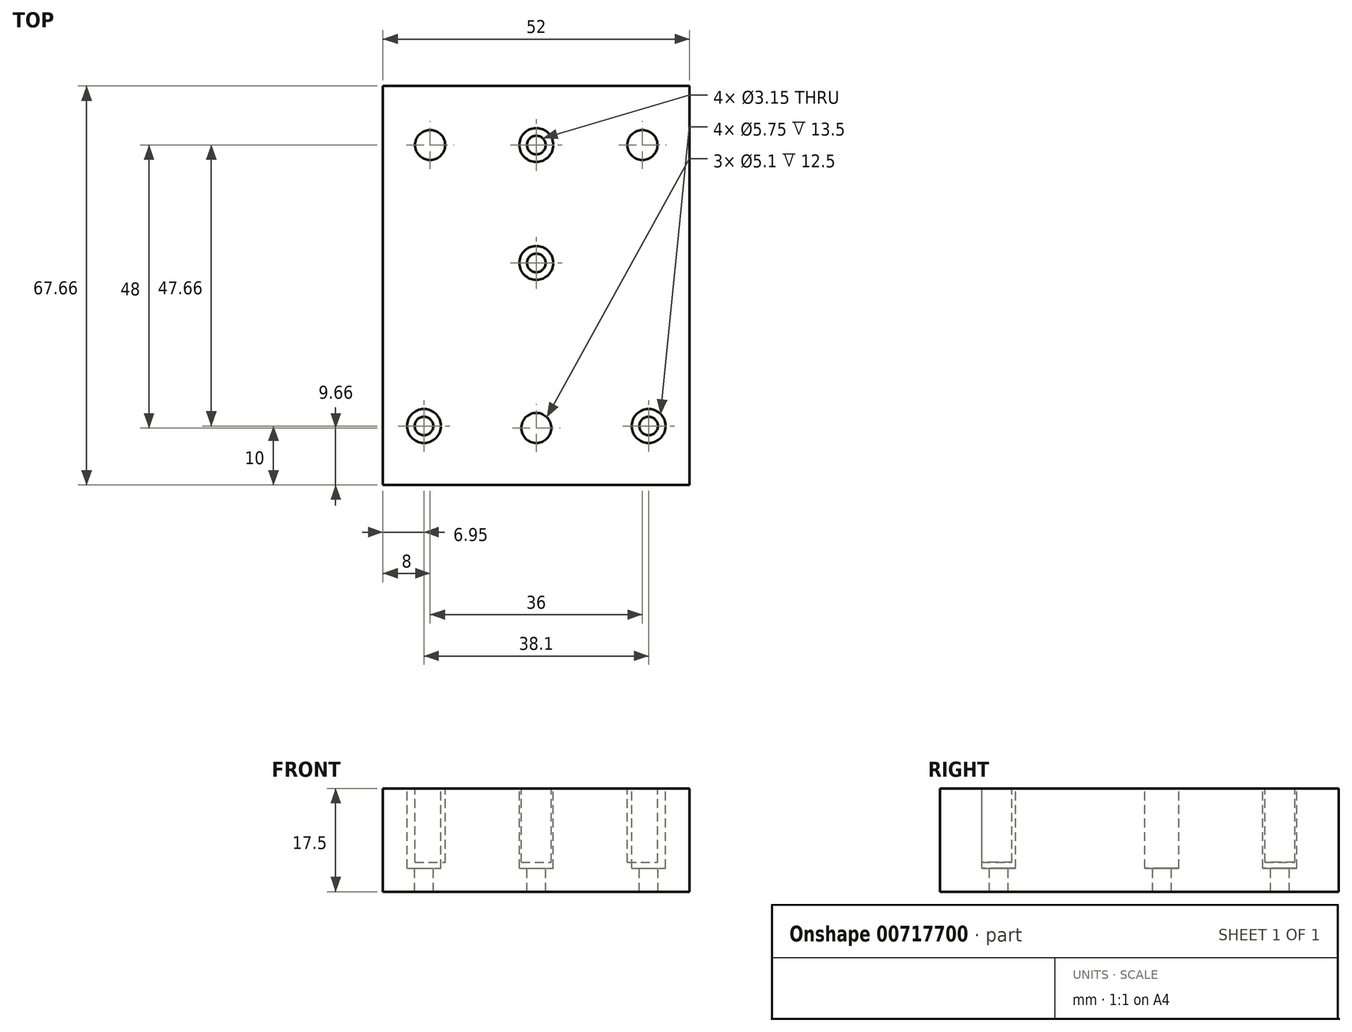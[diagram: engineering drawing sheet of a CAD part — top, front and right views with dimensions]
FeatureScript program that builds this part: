
annotation { "Feature Type Name" : "Feature", "Feature Type Description" : "" }
export const myFeature = defineFeature(function(context is Context, id is Id, definition is map)
    precondition{}
    {
        {
            var Q0;
            Q0=qCreatedBy(makeId("Top.planeOp"),FACE);
            var sketch = newSketch(context, id + "F0", { "sketchPlane" : qUnion([Q0])});
            skCircle(sketch, "E0", {"center": v(0, 0) * mm, "radius": 1.57 * mm});
            skCircle(sketch, "E1", {"center": v(0, -20) * mm, "radius": 1.57 * mm});
            skCircle(sketch, "E2", {"center": v(-19.05, 27.66) * mm, "radius": 1.58 * mm});
            skCircle(sketch, "E3", {"center": v(19.05, 27.66) * mm, "radius": 1.57 * mm});
            skSolve(sketch);
        }
        {
            var Q0;
            Q0=qCreatedBy(makeId("Top.planeOp"),FACE);
            var sketch = newSketch(context, id + "F1", { "sketchPlane" : qUnion([Q0])});
            skLineSegment(sketch, "E4.bottom", {"start": v(-26, -30) * mm, "end": v(26, -30) * mm});
            skLineSegment(sketch, "E4.top", {"start": v(-26, 37.66) * mm, "end": v(26, 37.66) * mm});
            skLineSegment(sketch, "E4.left", {"start": v(-26, -30) * mm, "end": v(-26, 37.66) * mm});
            skLineSegment(sketch, "E4.right", {"start": v(26, -30) * mm, "end": v(26, 37.66) * mm});
            skSolve(sketch);
        }
        {
            var Q0;
            Q0 = qSketchRegion(id + "F1", true);
            extrude(context, id + "F2", {"entities" : qUnion([Q0]), "depth" : 17.5 * mm, "offsetDistance" : 25 * mm});
        }
        {
            var Q0;
            Q0 = qSketchRegion(id + "F0", true);
            extrude(context, id + "F3", {"entities" : qUnion([Q0]), "operationType" : NewBodyOperationType.REMOVE, "oppositeDirection" : true, "depth" : -17.5 * mm, "offsetDistance" : 25 * mm});
        }
        {
            var Q0;
            Q0=makeQuery(id+"F2.opExtrude","CAP_FACE",FACE,{"disambiguationData":[OSD([sQuery(id+"F1.wireOp",EDGE,"E4.bottom"),sQuery(id+"F1.wireOp",EDGE,"E4.top"),sQuery(id+"F1.wireOp",EDGE,"E4.left"),sQuery(id+"F1.wireOp",EDGE,"E4.right")])],"isStart":true});
            var sketch = newSketch(context, id + "F4", { "sketchPlane" : qUnion([Q0])});
            skCircle(sketch, "E5", {"center": v(0, 0) * mm, "radius": 2.88 * mm});
            skCircle(sketch, "E6", {"center": v(19.05, -27.66) * mm, "radius": 2.88 * mm});
            skCircle(sketch, "E7", {"center": v(-19.05, -27.66) * mm, "radius": 2.88 * mm});
            skCircle(sketch, "E8", {"center": v(0, 20) * mm, "radius": 2.88 * mm});
            skSolve(sketch);
        }
        {
            var Q0;
            Q0 = qSketchRegion(id + "F4", true);
            extrude(context, id + "F5", {"entities" : qUnion([Q0]), "operationType" : NewBodyOperationType.REMOVE, "oppositeDirection" : true, "depth" : 13.5 * mm, "offsetDistance" : 25 * mm});
        }
        {
            var Q0;
            Q0=makeQuery(id+"F2.opExtrude","CAP_FACE",FACE,{"disambiguationData":[OSD([sQuery(id+"F1.wireOp",EDGE,"E4.bottom"),sQuery(id+"F1.wireOp",EDGE,"E4.top"),sQuery(id+"F1.wireOp",EDGE,"E4.left"),sQuery(id+"F1.wireOp",EDGE,"E4.right")])],"isStart":true});
            var sketch = newSketch(context, id + "F6", { "sketchPlane" : qUnion([Q0])});
            skCircle(sketch, "E9", {"center": v(0, -28) * mm, "radius": 2.55 * mm});
            skCircle(sketch, "E10", {"center": v(-18, 20) * mm, "radius": 2.55 * mm});
            skCircle(sketch, "E11", {"center": v(18, 20) * mm, "radius": 2.55 * mm});
            skSolve(sketch);
        }
        {
            var Q0;
            Q0 = qSketchRegion(id + "F6", true);
            extrude(context, id + "F7", {"entities" : qUnion([Q0]), "operationType" : NewBodyOperationType.REMOVE, "oppositeDirection" : true, "depth" : 12.5 * mm, "offsetDistance" : 25 * mm});
        }
        {
            var Q0;
            Q0=makeQuery(id+"F2.opExtrude","SWEPT_BODY",BODY,{"disambiguationData":[OSD([sQuery(id+"F1.wireOp",EDGE,"E4.bottom"),sQuery(id+"F1.wireOp",EDGE,"E4.top"),sQuery(id+"F1.wireOp",EDGE,"E4.left"),sQuery(id+"F1.wireOp",EDGE,"E4.right")])]});
            var Q1;
            Q1=makeQuery(id+"F2.opExtrude","CAP_EDGE",EDGE,{"disambiguationData":[OSD([sQuery(id+"F1.wireOp",EDGE,"E4.top")])],"isStart":false});
            var Q2;
            Q2=makeQuery(id+"F2.opExtrude","CAP_EDGE",EDGE,{"disambiguationData":[OSD([sQuery(id+"F1.wireOp",EDGE,"E4.left")])],"isStart":false});
            transform(context, id + "F8", {"entities" : qUnion([Q0]), "transformType" : TransformType.ROTATION, "transformAxis" : qUnion([Q2]), "angle" : 180 * degree, "makeCopy" : false});
        }
        {
            var Q0;
            Q0=makeQuery(id+"F2.opExtrude","SWEPT_BODY",BODY,{"disambiguationData":[OSD([sQuery(id+"F1.wireOp",EDGE,"E4.bottom"),sQuery(id+"F1.wireOp",EDGE,"E4.top"),sQuery(id+"F1.wireOp",EDGE,"E4.left"),sQuery(id+"F1.wireOp",EDGE,"E4.right")])]});
            var Q1;
            Q1=makeQuery(id+"F2.opExtrude","SWEPT_EDGE",EDGE,{"disambiguationData":[OSD([sQuery(id+"F1.wireOp",EDGE,"E4.top"),sQuery(id+"F1.wireOp",EDGE,"E4.left")])]});
            transform(context, id + "F9", {"entities" : qUnion([Q0]), "transformType" : TransformType.ROTATION, "transformAxis" : qUnion([Q1]), "angle" : 180 * degree, "makeCopy" : false});
        }
        {
            var Q0;
            Q0=makeQuery(id+"F2.opExtrude","CAP_EDGE",EDGE,{"disambiguationData":[OSD([sQuery(id+"F1.wireOp",EDGE,"E4.bottom")])],"isStart":true});
            cPoint(context, id + "F10", {"entities" : qUnion([Q0]), "parameter" : 0.5});
        }
        {
            var Q0;
            Q0=makeQuery(id+"F2.opExtrude","SWEPT_BODY",BODY,{"disambiguationData":[OSD([sQuery(id+"F1.wireOp",EDGE,"E4.bottom"),sQuery(id+"F1.wireOp",EDGE,"E4.top"),sQuery(id+"F1.wireOp",EDGE,"E4.left"),sQuery(id+"F1.wireOp",EDGE,"E4.right")])]});
            var Q1;
            Q1=qCreatedBy(makeId("Origin.pointOp"),VERTEX);
            var Q2;
            Q2 = qCreatedBy(id + "F10" ,VERTEX);
            transform(context, id + "F11", {"entities" : qUnion([Q0]), "transformType" : TransformType.TRANSLATION_ENTITY, "oppositeDirectionEntity" : true, "transformLine" : qUnion([Q1, Q2]), "makeCopy" : false});
        }
    });
